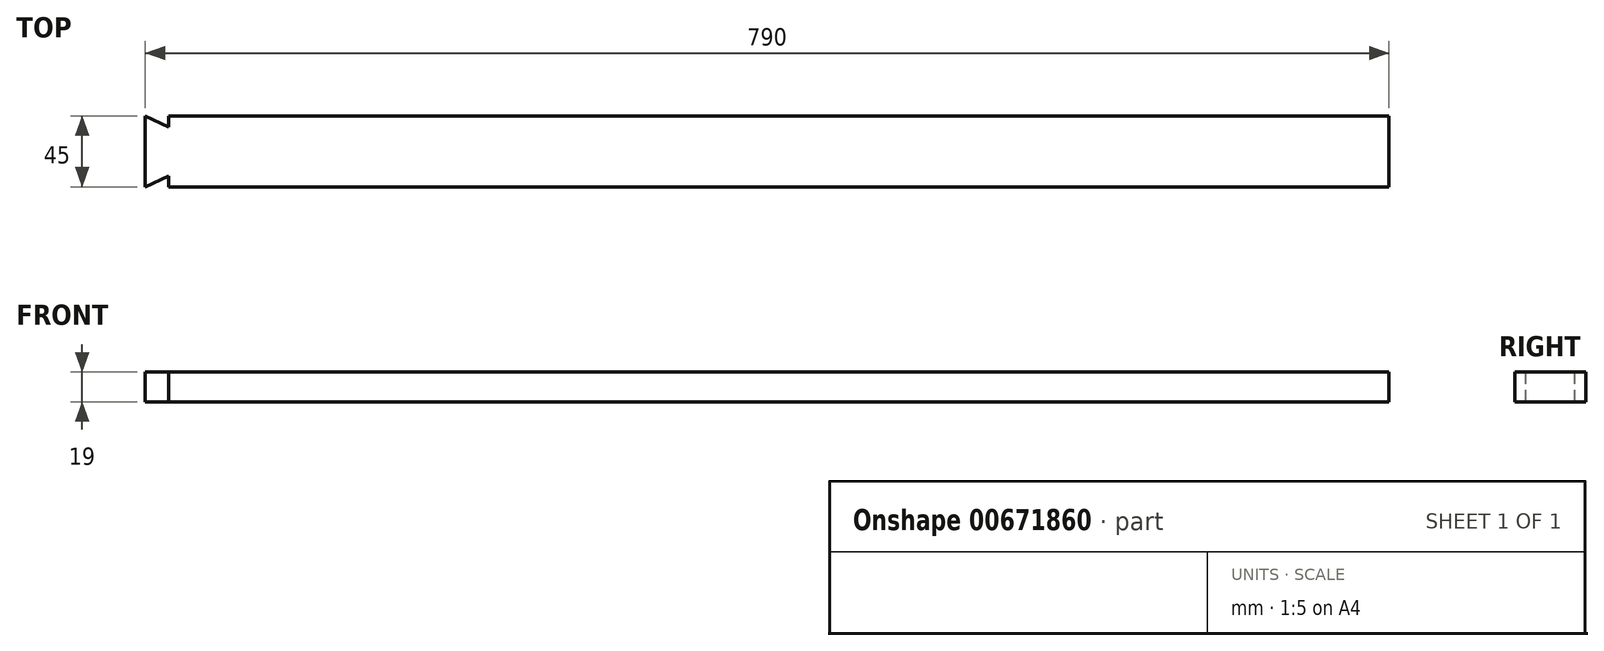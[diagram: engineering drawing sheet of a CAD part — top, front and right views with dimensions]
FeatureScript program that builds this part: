
annotation { "Feature Type Name" : "Feature", "Feature Type Description" : "" }
export const myFeature = defineFeature(function(context is Context, id is Id, definition is map)
    precondition{}
    {
        {
            var Q0;
            Q0=qCreatedBy(makeId("Top.planeOp"),FACE);
            var sketch = newSketch(context, id + "F0", { "sketchPlane" : qUnion([Q0])});
            skLineSegment(sketch, "E0.bottom", {"start": v(-395, 22.5) * mm, "end": v(395, 22.5) * mm});
            skLineSegment(sketch, "E0.top", {"start": v(-395, -22.5) * mm, "end": v(395, -22.5) * mm});
            skLineSegment(sketch, "E0.left", {"start": v(-395, 22.5) * mm, "end": v(-395, -22.5) * mm});
            skLineSegment(sketch, "E0.right", {"start": v(395, 22.5) * mm, "end": v(395, -22.5) * mm});
            skPoint(sketch, "E0.middle", {"position": v(0, 0) * mm});
            skLineSegment(sketch, "E1", {"start": v(-395, 22.5) * mm, "end": v(-380, 22.5) * mm});
            skSolve(sketch);
        }
        {
            var Q0;
            Q0=makeQuery(id+"F0.imprint","IMPRINT",FACE,{"disambiguationData":[TD([[makeQuery(id+"F0.imprint","IMPRINT",EDGE,{"derivedFrom":sQuery(id+"F0.wireOp",EDGE,"E0.bottom")}),-1.0]])]});
            extrude(context, id + "F1", {"entities" : qUnion([Q0]), "depth" : 19 * mm, "offsetDistance" : 25 * mm});
        }
        {
            var Q0;
            Q0=makeQuery(id+"F1.opExtrude","CAP_FACE",FACE,{"disambiguationData":[OSD([sQuery(id+"F0.wireOp",EDGE,"E0.bottom"),sQuery(id+"F0.wireOp",EDGE,"E0.top"),sQuery(id+"F0.wireOp",EDGE,"E0.left"),sQuery(id+"F0.wireOp",EDGE,"E0.right"),sQuery(id+"F0.wireOp",EDGE,"E1")])],"isStart":false});
            var sketch = newSketch(context, id + "F2", { "sketchPlane" : qUnion([Q0])});
            skLineSegment(sketch, "E2", {"start": v(-380, 22.5) * mm, "end": v(-380, 15.5) * mm});
            skLineSegment(sketch, "E3", {"start": v(-380, 15.5) * mm, "end": v(-395, 22.5) * mm});
            skLineSegment(sketch, "E4", {"start": v(-380, -22.5) * mm, "end": v(-380, -15.5) * mm});
            skPoint(sketch, "E4.startSnap0", {"position": v(-380, 19) * mm});
            skLineSegment(sketch, "E5", {"start": v(-380, -15.5) * mm, "end": v(-395, -22.5) * mm});
            skLineSegment(sketch, "E6", {"start": v(0, 22.5) * mm, "end": v(0, -22.5) * mm});
            skSolve(sketch);
        }
        {
            var Q0;
            {var subQ0=sQuery(id+"F2.wireOp",EDGE,"E2");Q0=makeQuery(id+"F2.imprint","IMPRINT",FACE,{"disambiguationData":[TD([[makeQuery(id+"F2.imprint","IMPRINT",EDGE,{"derivedFrom":subQ0}),-1.0]])]});}
            var Q1;
            {var subQ0=sQuery(id+"F2.wireOp",EDGE,"E4");Q1=makeQuery(id+"F2.imprint","IMPRINT",FACE,{"disambiguationData":[TD([[makeQuery(id+"F2.imprint","IMPRINT",EDGE,{"derivedFrom":subQ0}),1.0]])]});}
            extrude(context, id + "F3", {"entities" : qUnion([Q0, Q1]), "operationType" : NewBodyOperationType.REMOVE, "endBound" : BoundingType.THROUGH_ALL, "oppositeDirection" : true, "depth" : 25 * mm, "offsetDistance" : 25 * mm});
        }
    });
